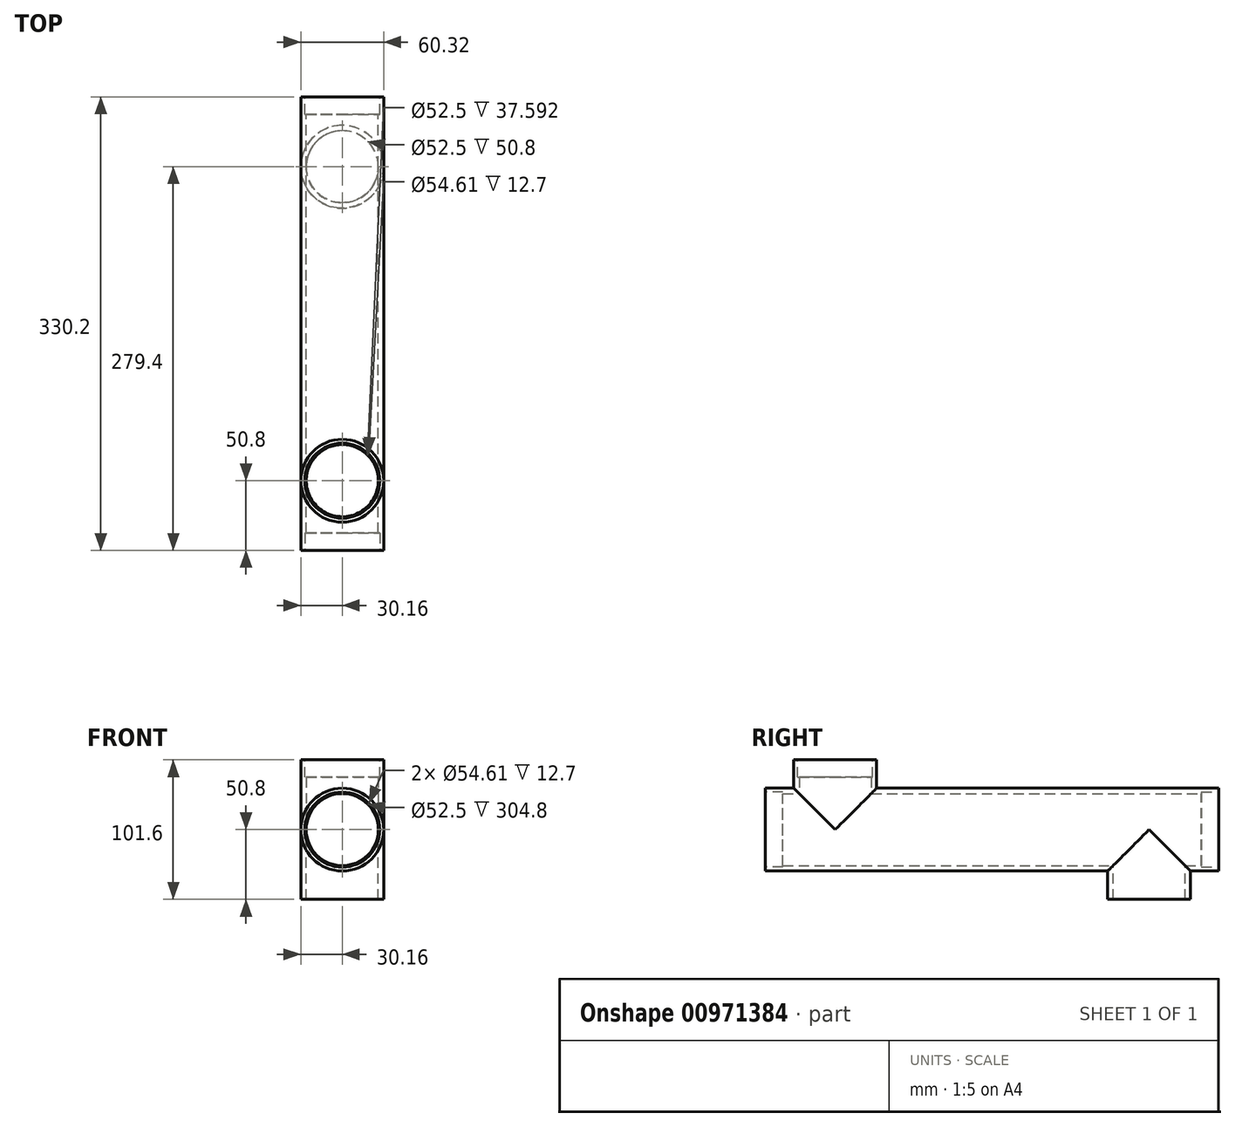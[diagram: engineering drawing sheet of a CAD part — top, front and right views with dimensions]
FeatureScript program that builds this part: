
annotation { "Feature Type Name" : "Feature", "Feature Type Description" : "" }
export const myFeature = defineFeature(function(context is Context, id is Id, definition is map)
    precondition{}
    {
        {
            var Q0;
            Q0=qCreatedBy(makeId("Front.planeOp"),FACE);
            var sketch = newSketch(context, id + "F0", { "sketchPlane" : qUnion([Q0])});
            skCircle(sketch, "E0", {"center": v(0, 0) * mm, "radius": 26.25 * mm});
            skCircle(sketch, "E1", {"center": v(0, 0) * mm, "radius": 30.16 * mm});
            skSolve(sketch);
        }
        {
            var Q0;
            Q0=makeQuery(id+"F0.imprint","IMPRINT",FACE,{"disambiguationData":[TD([[makeQuery(id+"F0.imprint","IMPRINT",EDGE,{"derivedFrom":sQuery(id+"F0.wireOp",EDGE,"E0")}),-1.0]])]});
            extrude(context, id + "F1", {"entities" : qUnion([Q0]), "endBound" : BoundingType.SYMMETRIC, "depth" : 330.2 * mm, "offsetDistance" : 25.4 * mm});
        }
        {
            var Q0;
            Q0=qCreatedBy(makeId("Top.planeOp"),FACE);
            var sketch = newSketch(context, id + "F2", { "sketchPlane" : qUnion([Q0])});
            skLineSegment(sketch, "E2", {"start": v(0, 0) * mm, "end": v(0, -114.3) * mm});
            skCircle(sketch, "E3", {"center": v(0, -114.3) * mm, "radius": 30.16 * mm});
            skCircle(sketch, "E4", {"center": v(0, -114.3) * mm, "radius": 26.25 * mm});
            skSolve(sketch);
        }
        {
            var Q0;
            Q0=makeQuery(id+"F2.imprint","IMPRINT",FACE,{"disambiguationData":[TD([[makeQuery(id+"F2.imprint","IMPRINT",EDGE,{"derivedFrom":sQuery(id+"F2.wireOp",EDGE,"E3")}),1.0]])]});
            extrude(context, id + "F3", {"entities" : qUnion([Q0]), "operationType" : NewBodyOperationType.ADD, "depth" : 50.8 * mm, "offsetDistance" : 25.4 * mm});
        }
        {
            var Q0;
            Q0=qCreatedBy(makeId("Top.planeOp"),FACE);
            var sketch = newSketch(context, id + "F4", { "sketchPlane" : qUnion([Q0])});
            skCircle(sketch, "E5", {"center": v(0, 114.3) * mm, "radius": 30.16 * mm});
            skCircle(sketch, "E6", {"center": v(0, 114.3) * mm, "radius": 26.25 * mm});
            skLineSegment(sketch, "E7", {"start": v(0, 0) * mm, "end": v(0, 114.3) * mm});
            skSolve(sketch);
        }
        {
            var Q0;
            Q0 = qSketchRegion(id + "F4", true);
            extrude(context, id + "F5", {"entities" : qUnion([Q0]), "operationType" : NewBodyOperationType.ADD, "oppositeDirection" : true, "depth" : 50.8 * mm, "offsetDistance" : 25.4 * mm});
        }
        {
            var Q0;
            Q0=makeQuery(id+"F1.opExtrude","CAP_FACE",FACE,{"disambiguationData":[OSD([sQuery(id+"F0.wireOp",EDGE,"E0"),sQuery(id+"F0.wireOp",EDGE,"E1")])],"isStart":true});
            var sketch = newSketch(context, id + "F6", { "sketchPlane" : qUnion([Q0])});
            skCircle(sketch, "E8", {"center": v(0, 0) * mm, "radius": 26.25 * mm});
            skSolve(sketch);
        }
        {
            var Q0;
            Q0=makeQuery(id+"F6.imprint","IMPRINT",FACE,{"disambiguationData":[TD([[makeQuery(id+"F6.imprint","IMPRINT",EDGE,{"derivedFrom":sQuery(id+"F6.wireOp",EDGE,"E8")}),-1.0]])]});
            extrude(context, id + "F7", {"entities" : qUnion([Q0]), "operationType" : NewBodyOperationType.REMOVE, "oppositeDirection" : true, "depth" : 304.8 * mm, "offsetDistance" : 25.4 * mm});
        }
        {
            var Q0;
            Q0=makeQuery(id+"F3.opExtrude","CAP_FACE",FACE,{"disambiguationData":[OSD([sQuery(id+"F2.wireOp",EDGE,"E3"),sQuery(id+"F2.wireOp",EDGE,"E4")])],"isStart":false});
            var sketch = newSketch(context, id + "F8", { "sketchPlane" : qUnion([Q0])});
            skCircle(sketch, "E9", {"center": v(0, -114.3) * mm, "radius": 26.25 * mm});
            skSolve(sketch);
        }
        {
            var Q0;
            Q0=makeQuery(id+"F8.imprint","IMPRINT",FACE,{"disambiguationData":[TD([[makeQuery(id+"F8.imprint","IMPRINT",EDGE,{"derivedFrom":sQuery(id+"F8.wireOp",EDGE,"E9")}),1.0]])]});
            extrude(context, id + "F9", {"entities" : qUnion([Q0]), "operationType" : NewBodyOperationType.REMOVE, "oppositeDirection" : true, "depth" : 50.3 * mm, "offsetDistance" : 25.4 * mm});
        }
        {
            var Q0;
            Q0=makeQuery(id+"F5.opExtrude","CAP_FACE",FACE,{"disambiguationData":[OSD([sQuery(id+"F4.wireOp",EDGE,"E5"),sQuery(id+"F4.wireOp",EDGE,"E6")])],"isStart":false});
            var sketch = newSketch(context, id + "F10", { "sketchPlane" : qUnion([Q0])});
            skCircle(sketch, "E10", {"center": v(0, -114.3) * mm, "radius": 26.25 * mm});
            skSolve(sketch);
        }
        {
            var Q0;
            Q0=makeQuery(id+"F10.imprint","IMPRINT",FACE,{"disambiguationData":[TD([[makeQuery(id+"F10.imprint","IMPRINT",EDGE,{"derivedFrom":sQuery(id+"F10.wireOp",EDGE,"E10")}),-1.0]])]});
            extrude(context, id + "F11", {"entities" : qUnion([Q0]), "operationType" : NewBodyOperationType.REMOVE, "oppositeDirection" : true, "depth" : 50.8 * mm, "offsetDistance" : 25.4 * mm});
        }
        {
            var Q0;
            Q0=makeQuery(id+"F1.opExtrude","CAP_FACE",FACE,{"disambiguationData":[OSD([sQuery(id+"F0.wireOp",EDGE,"E0"),sQuery(id+"F0.wireOp",EDGE,"E1")])],"isStart":true});
            var sketch = newSketch(context, id + "F12", { "sketchPlane" : qUnion([Q0])});
            skCircle(sketch, "E11", {"center": v(0, 0) * mm, "radius": 27.94 * mm});
            skSolve(sketch);
        }
        {
            var Q0;
            Q0=makeQuery(id+"F12.imprint","IMPRINT",FACE,{"disambiguationData":[TD([[makeQuery(id+"F12.imprint","IMPRINT",EDGE,{"derivedFrom":makeQuery(id+"F1.opExtrude","CAP_EDGE",EDGE,{"disambiguationData":[OSD([sQuery(id+"F0.wireOp",EDGE,"E0")])],"isStart":true})}),-1.0]])]});
            extrude(context, id + "F13", {"entities" : qUnion([Q0]), "operationType" : NewBodyOperationType.REMOVE, "oppositeDirection" : true, "depth" : 12.7 * mm, "offsetDistance" : 25.4 * mm});
        }
        {
            var Q0;
            Q0=makeQuery(id+"F1.opExtrude","CAP_FACE",FACE,{"disambiguationData":[OSD([sQuery(id+"F0.wireOp",EDGE,"E0"),sQuery(id+"F0.wireOp",EDGE,"E1")])],"isStart":false});
            var sketch = newSketch(context, id + "F14", { "sketchPlane" : qUnion([Q0])});
            skCircle(sketch, "E12", {"center": v(0, 0) * mm, "radius": 27.3 * mm});
            skSolve(sketch);
        }
        {
            var Q0;
            Q0 = qSketchRegion(id + "F14", true);
            extrude(context, id + "F15", {"entities" : qUnion([Q0]), "operationType" : NewBodyOperationType.REMOVE, "oppositeDirection" : true, "depth" : 12.7 * mm, "offsetDistance" : 25.4 * mm});
        }
        {
            var Q0;
            Q0=makeQuery(id+"F1.opExtrude","CAP_FACE",FACE,{"disambiguationData":[OSD([sQuery(id+"F0.wireOp",EDGE,"E0"),sQuery(id+"F0.wireOp",EDGE,"E1")])],"isStart":true});
            var sketch = newSketch(context, id + "F16", { "sketchPlane" : qUnion([Q0])});
            skCircle(sketch, "E13", {"center": v(0, 0) * mm, "radius": 27.3 * mm});
            skSolve(sketch);
        }
        {
            var Q0;
            Q0=makeQuery(id+"F16.imprint","IMPRINT",FACE,{"disambiguationData":[TD([[makeQuery(id+"F16.imprint","IMPRINT",EDGE,{"derivedFrom":sQuery(id+"F16.wireOp",EDGE,"E13")}),1.0]])]});
            var Q1;
            Q1=sQuery(id+"F16.wireOp",EDGE,"E13");
            extrude(context, id + "F17", {"entities" : qUnion([Q0]), "operationType" : NewBodyOperationType.REMOVE, "surfaceEntities" : qUnion([Q1]), "oppositeDirection" : true, "depth" : 12.7 * mm, "offsetDistance" : 25.4 * mm});
        }
        {
            var Q0;
            Q0=makeQuery(id+"F3.opExtrude","CAP_FACE",FACE,{"disambiguationData":[OSD([sQuery(id+"F2.wireOp",EDGE,"E3"),sQuery(id+"F2.wireOp",EDGE,"E4")])],"isStart":false});
            var sketch = newSketch(context, id + "F18", { "sketchPlane" : qUnion([Q0])});
            skCircle(sketch, "E14", {"center": v(0, -114.3) * mm, "radius": 27.3 * mm});
            skSolve(sketch);
        }
        {
            var Q0;
            Q0=makeQuery(id+"F18.imprint","IMPRINT",FACE,{"disambiguationData":[TD([[makeQuery(id+"F18.imprint","IMPRINT",EDGE,{"derivedFrom":sQuery(id+"F18.wireOp",EDGE,"E14")}),1.0]])]});
            var Q1;
            Q1=sQuery(id+"F18.wireOp",EDGE,"E14");
            extrude(context, id + "F19", {"entities" : qUnion([Q0]), "operationType" : NewBodyOperationType.REMOVE, "surfaceEntities" : qUnion([Q1]), "oppositeDirection" : true, "depth" : 12.7 * mm, "offsetDistance" : 25.4 * mm});
        }
        {
            var Q0;
            Q0=makeQuery(id+"F1.opExtrude","CAP_FACE",FACE,{"disambiguationData":[OSD([sQuery(id+"F0.wireOp",EDGE,"E0"),sQuery(id+"F0.wireOp",EDGE,"E1")])],"isStart":false});
            var sketch = newSketch(context, id + "F20", { "sketchPlane" : qUnion([Q0])});
            skCircle(sketch, "E15", {"center": v(0, 0) * mm, "radius": 26.25 * mm});
            skSolve(sketch);
        }
        {
            var Q0;
            Q0=makeQuery(id+"F20.imprint","IMPRINT",FACE,{"disambiguationData":[TD([[makeQuery(id+"F20.imprint","IMPRINT",EDGE,{"derivedFrom":sQuery(id+"F20.wireOp",EDGE,"E15")}),1.0]])]});
            extrude(context, id + "F21", {"entities" : qUnion([Q0]), "operationType" : NewBodyOperationType.REMOVE, "endBound" : BoundingType.THROUGH_ALL, "oppositeDirection" : true, "depth" : 25.4 * mm, "offsetDistance" : 25.4 * mm});
        }
    });
